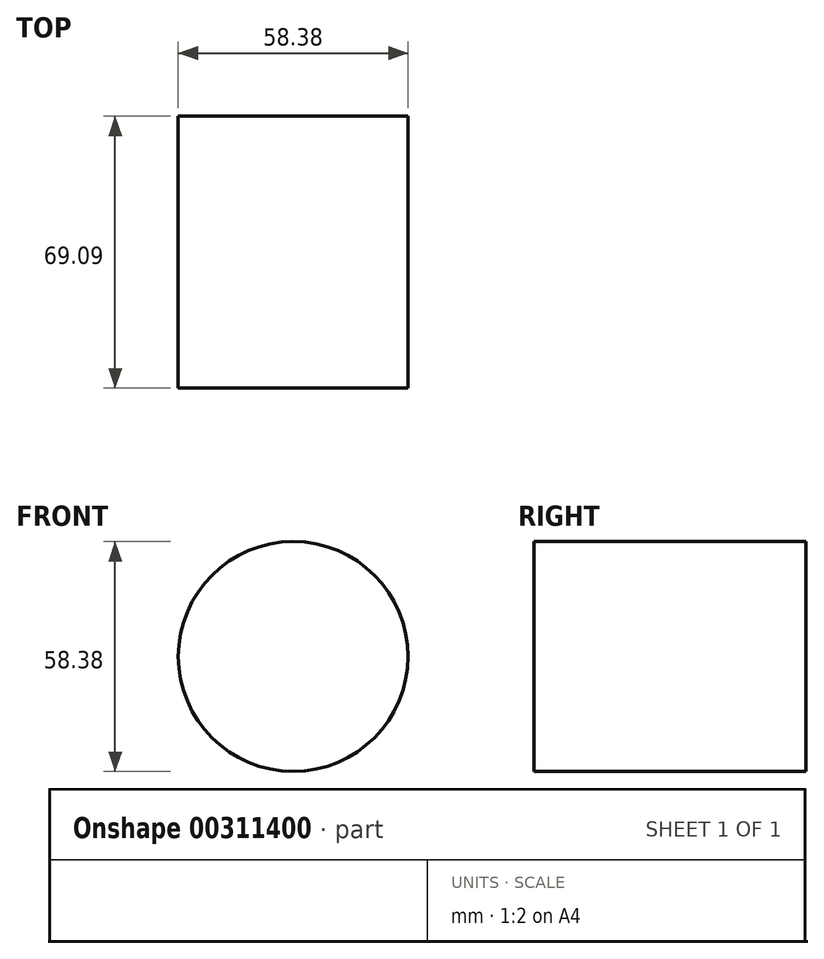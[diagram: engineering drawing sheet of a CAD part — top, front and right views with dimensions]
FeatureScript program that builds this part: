
annotation { "Feature Type Name" : "Feature", "Feature Type Description" : "" }
export const myFeature = defineFeature(function(context is Context, id is Id, definition is map)
    precondition{}
    {
        {
            var Q0;
            Q0=qCreatedBy(makeId("Front.planeOp"),FACE);
            var sketch = newSketch(context, id + "F0", { "sketchPlane" : qUnion([Q0])});
            skCircle(sketch, "E0", {"center": v(0, 0) * mm, "radius": 29.19 * mm});
            skSolve(sketch);
        }
        {
            var Q0;
            Q0=makeQuery(id+"F0.imprint","IMPRINT",FACE,{"disambiguationData":[TD([[makeQuery(id+"F0.imprint","IMPRINT",EDGE,{"derivedFrom":sQuery(id+"F0.wireOp",EDGE,"E0")}),1.0]])]});
            extrude(context, id + "F1", {"entities" : qUnion([Q0]), "depth" : 69.1 * mm});
        }
    });
